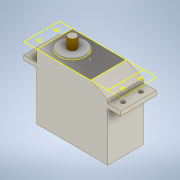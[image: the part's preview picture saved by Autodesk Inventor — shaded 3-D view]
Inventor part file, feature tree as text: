
AUTODESK INVENTOR PART (.ipt)
format: ipt  version: 2020.3 (Build 243373000, 373)  size: 406,528 bytes
history: native  units: mm
features: sketch x8, extrude x7, projected_geometry x6, chamfer x1, pattern_circular x1
ambient origin geometry x8: Origin, YZ Plane, XZ Plane, XY Plane, X Axis, Y Axis, Z Axis, Center Point
bodies: Solid1 (feature_tree)
feature tree (23):
  extrude  "Extrusion1"  Depth=20.1mm
  extrude  "Extrusion2"  Depth=55.0mm
  extrude  "Extrusion3"  TaperAngle=0.0deg  [1 undecoded]
  extrude  "Extrusion4"  Depth=10.0mm TaperAngle=0.0deg
  extrude  "Extrusion5"  Depth=0.7mm TaperAngle=0.0deg
  extrude  "Extrusion6"  Depth=6.0mm TaperAngle=0.0deg
  chamfer  "Chamfer1"  Distance=9.75mm
  extrude  "Extrusion7"  TaperAngle=45.0deg  [1 undecoded]
  pattern_circular  "Circular Pattern1"  Count=80 Angle=360.0deg
  sketch  "Sketch8"  dims[d24=10.0mm d25=0.0mm d26=800.0mm d27=360.0deg]
  sketch  "Sketch1"  dims[d0=40.2mm d1=20.1mm]
  sketch  "Sketch2"  dims[d2=27.7mm d3=0.0mm d4=55.0mm]
  sketch  "Sketch3"  dims[d5=2.5mm d6=0.0mm d8=0.0mm d9=0.0mm]
  projected_geometry  "Projected Loop1"
  sketch  "Sketch4"  dims[d10=36.8mm d11=10.0mm d12=0.0mm]
  sketch  "Sketch5"  dims[d13=15.0mm d14=0.7mm d15=0.0mm]
  sketch  "Sketch6"  dims[d16=4.5mm d17=6.0mm d18=0.0mm d19=9.75mm d20=2.0mm d21=4.363323mm]
  sketch  "Sketch7"  dims[d22=0.1mm d23=45.0deg]
  projected_geometry  "Projected Loop2"
  projected_geometry  "Projected Loop3"
  projected_geometry  "Projected Loop4"
  projected_geometry  "Projected Loop5"
  projected_geometry  "Projected Loop6"
note: 2 required parameter values undecoded (feature->parameter linkage not recoverable at this tier; creation-order binding heuristic only, values carry confidence <= 0.55)
